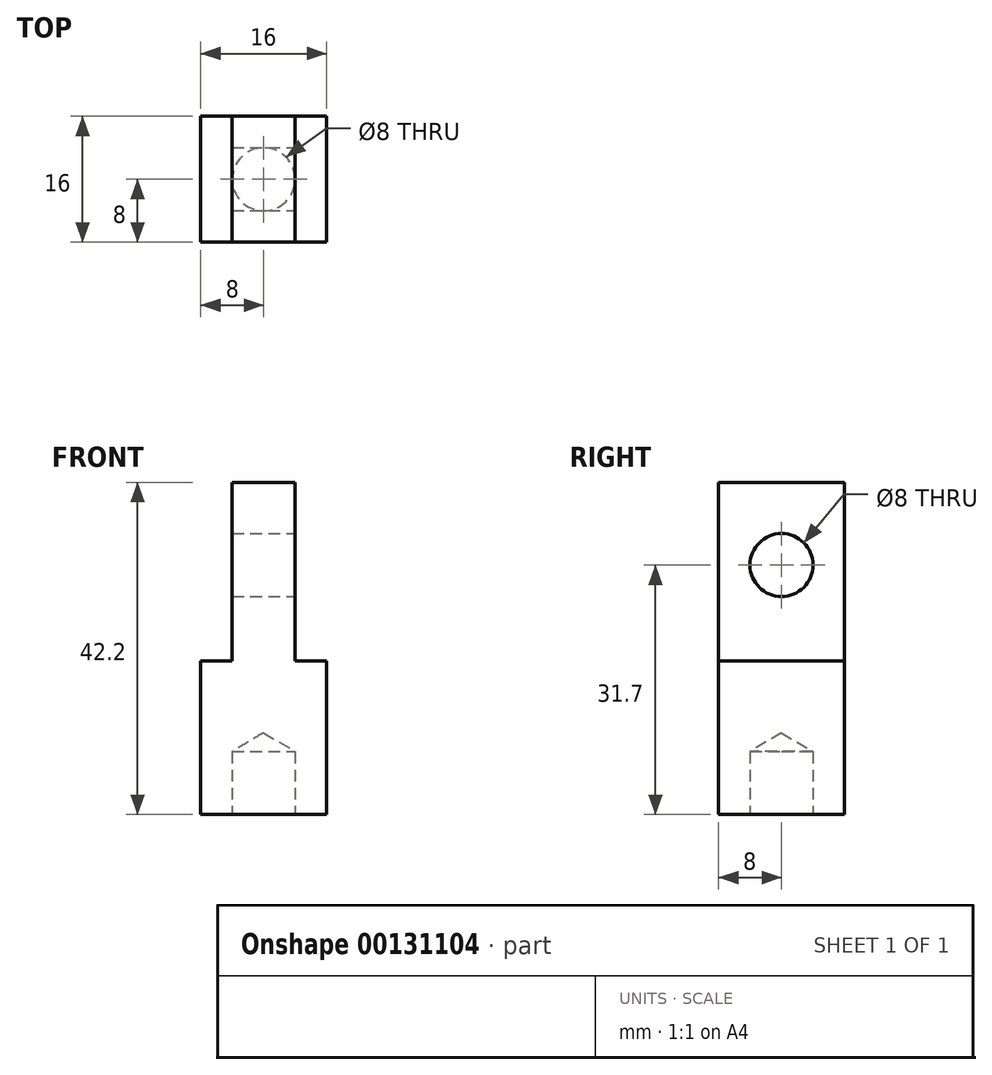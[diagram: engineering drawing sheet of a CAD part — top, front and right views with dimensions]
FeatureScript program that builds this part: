
annotation { "Feature Type Name" : "Feature", "Feature Type Description" : "" }
export const myFeature = defineFeature(function(context is Context, id is Id, definition is map)
    precondition{}
    {
        {
            var Q0;
            Q0=qCreatedBy(makeId("Front.planeOp"),FACE);
            var sketch = newSketch(context, id + "F0", { "sketchPlane" : qUnion([Q0])});
            skLineSegment(sketch, "E0.bottom", {"start": v(8, -9.75) * mm, "end": v(-8, -9.75) * mm});
            skLineSegment(sketch, "E0.top", {"start": v(8, 9.75) * mm, "end": v(4, 9.75) * mm});
            skLineSegment(sketch, "E0.left", {"start": v(8, -9.75) * mm, "end": v(8, 9.75) * mm});
            skLineSegment(sketch, "E0.right", {"start": v(-8, -9.75) * mm, "end": v(-8, 9.75) * mm});
            skPoint(sketch, "E0.middle", {"position": v(0, 0) * mm});
            skLineSegment(sketch, "E1", {"start": v(0, 9.75) * mm, "end": v(0, 32.45) * mm, "construction": true});
            skLineSegment(sketch, "E2", {"start": v(0, 32.45) * mm, "end": v(4, 32.45) * mm});
            skLineSegment(sketch, "E3", {"start": v(0, 32.45) * mm, "end": v(-4, 32.45) * mm});
            skLineSegment(sketch, "E4", {"start": v(-4, 32.45) * mm, "end": v(-4, 9.75) * mm});
            skLineSegment(sketch, "E5", {"start": v(4, 32.45) * mm, "end": v(4, 9.75) * mm});
            skLineSegment(sketch, "E6.trimOffspring", {"start": v(-4, 9.75) * mm, "end": v(-8, 9.75) * mm});
            skSolve(sketch);
        }
        {
            var Q0;
            Q0=makeQuery(id+"F0.imprint","IMPRINT",FACE,{"disambiguationData":[TD([[makeQuery(id+"F0.imprint","IMPRINT",EDGE,{"derivedFrom":sQuery(id+"F0.wireOp",EDGE,"E0.bottom")}),-1.0]])]});
            extrude(context, id + "F1", {"entities" : qUnion([Q0]), "depth" : 16 * mm});
        }
        {
            var Q0;
            Q0=makeQuery(id+"F1.opExtrude","SWEPT_FACE",FACE,{"disambiguationData":[OSD([sQuery(id+"F0.wireOp",EDGE,"E5")])]});
            var sketch = newSketch(context, id + "F2", { "sketchPlane" : qUnion([Q0])});
            skPoint(sketch, "E7", {"position": v(-8, 21.95) * mm});
            skPoint(sketch, "E7.positionSnap0", {"position": v(-8, 32.45) * mm});
            skSolve(sketch);
        }
        {
            var Q0;
            Q0=sQuery(id+"F2.wireOp",VERTEX,"E7");
            var Q1;
            Q1=makeQuery(id+"F1.opExtrude","SWEPT_BODY",BODY,{"disambiguationData":[OSD([sQuery(id+"F0.wireOp",EDGE,"E0.bottom"),sQuery(id+"F0.wireOp",EDGE,"E0.top"),sQuery(id+"F0.wireOp",EDGE,"E0.left"),sQuery(id+"F0.wireOp",EDGE,"E0.right"),sQuery(id+"F0.wireOp",EDGE,"E2"),sQuery(id+"F0.wireOp",EDGE,"E3"),sQuery(id+"F0.wireOp",EDGE,"E4"),sQuery(id+"F0.wireOp",EDGE,"E5"),sQuery(id+"F0.wireOp",EDGE,"E6.trimOffspring")])]});
            hole(context, id + "F3", {"style" : HoleStyle.SIMPLE, "endStyle" : HoleEndStyle.THROUGH, "holeDiameter" : 8 * mm, "locations" : qUnion([Q0]), "scope" : qUnion([Q1]), "isTappedThrough" : true});
        }
        {
            var Q0;
            Q0=makeQuery(id+"F1.opExtrude","SWEPT_FACE",FACE,{"disambiguationData":[OSD([sQuery(id+"F0.wireOp",EDGE,"E0.bottom")])]});
            var sketch = newSketch(context, id + "F4", { "sketchPlane" : qUnion([Q0])});
            skPoint(sketch, "E8", {"position": v(0, 8) * mm});
            skPoint(sketch, "E8.positionSnap0", {"position": v(0, 0) * mm});
            skPoint(sketch, "E8.positionSnap1", {"position": v(8, 8) * mm});
            skSolve(sketch);
        }
        {
            var Q0;
            Q0=sQuery(id+"F4.wireOp",VERTEX,"E8");
            var Q1;
            Q1=makeQuery(id+"F1.opExtrude","SWEPT_BODY",BODY,{"disambiguationData":[OSD([sQuery(id+"F0.wireOp",EDGE,"E0.bottom"),sQuery(id+"F0.wireOp",EDGE,"E0.top"),sQuery(id+"F0.wireOp",EDGE,"E0.left"),sQuery(id+"F0.wireOp",EDGE,"E0.right"),sQuery(id+"F0.wireOp",EDGE,"E2"),sQuery(id+"F0.wireOp",EDGE,"E3"),sQuery(id+"F0.wireOp",EDGE,"E4"),sQuery(id+"F0.wireOp",EDGE,"E5"),sQuery(id+"F0.wireOp",EDGE,"E6.trimOffspring")])]});
            hole(context, id + "F5", {"style" : HoleStyle.SIMPLE, "endStyle" : HoleEndStyle.BLIND, "holeDiameter" : 8 * mm, "holeDepth" : 8 * mm, "locations" : qUnion([Q0]), "scope" : qUnion([Q1])});
        }
    });
